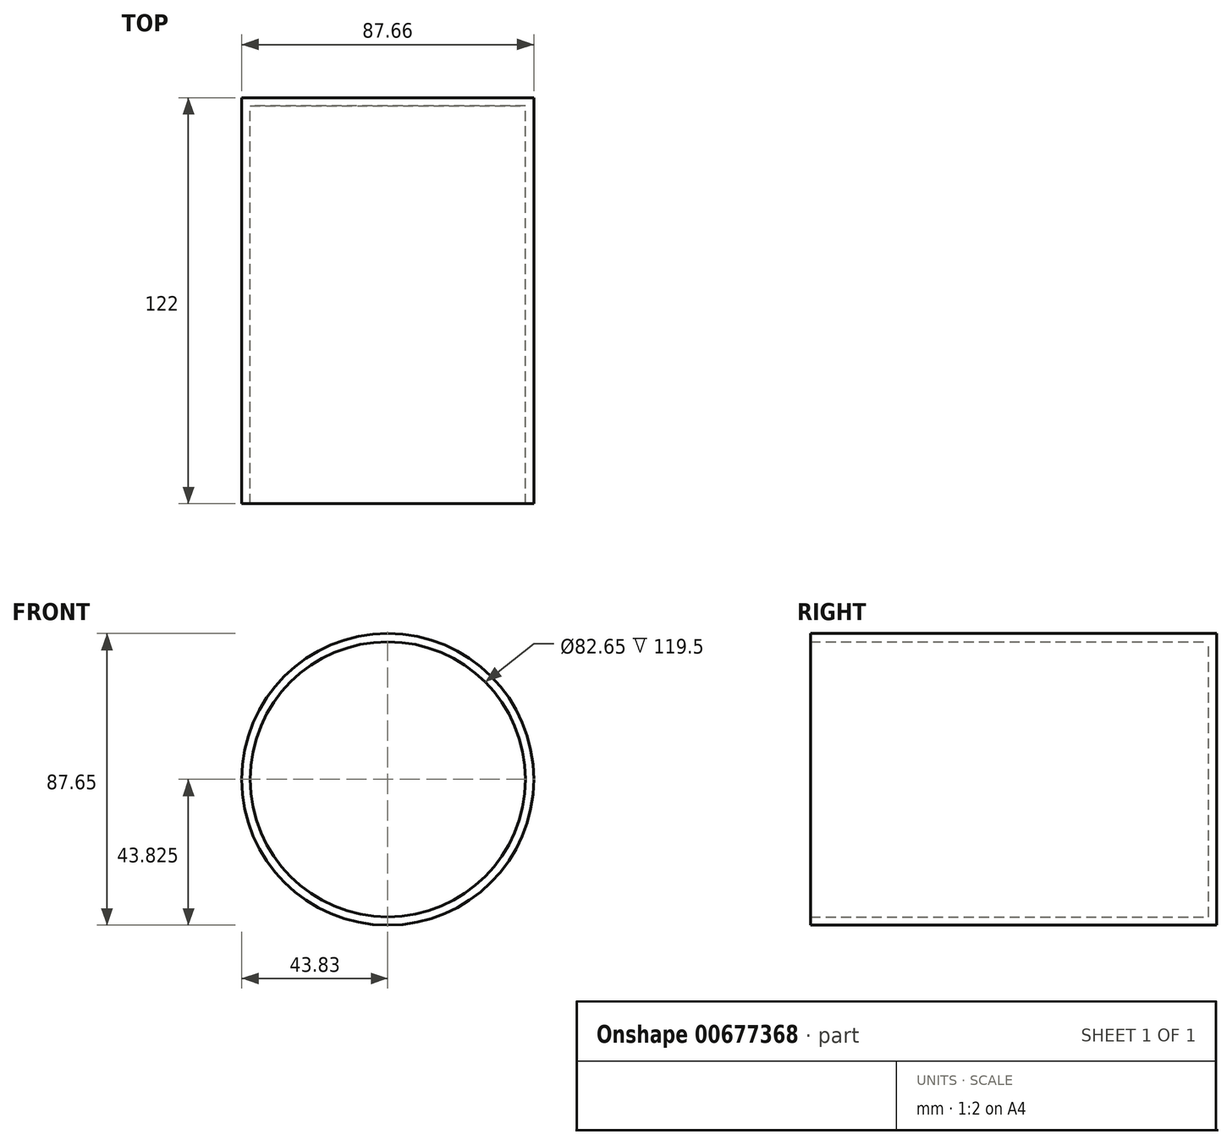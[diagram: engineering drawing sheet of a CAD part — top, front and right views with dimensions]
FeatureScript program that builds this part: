
annotation { "Feature Type Name" : "Feature", "Feature Type Description" : "" }
export const myFeature = defineFeature(function(context is Context, id is Id, definition is map)
    precondition{}
    {
        {
            var Q0;
            Q0=qCreatedBy(makeId("Front.planeOp"),FACE);
            var sketch = newSketch(context, id + "F0", { "sketchPlane" : qUnion([Q0])});
            skArc(sketch, "E0", {"start": v(20.21, 43.5) * mm, "mid": v(-20.49, 89.62) * mm, "end": v(-55.74, 39.2) * mm});
            skLineSegment(sketch, "E1", {"start": v(57.99, 97.4) * mm, "end": v(106.8, 16.13) * mm});
            skFitSpline(sketch, "E2", {"points": [v(-71.55, -93.28) * mm, v(-76.06, -16.4) * mm, v(10.86, -17.02) * mm], "startDerivative": vector(-52.45, 197.28) * mm, "endDerivative": vector(214.59, -42.33) * mm});
            skFitSpline(sketch, "E3.MirrorCS", {"points": [v(-71.55, 93.28) * mm, v(-76.06, 16.4) * mm, v(10.86, 17.02) * mm], "startDerivative": vector(-52.45, -197.28) * mm, "endDerivative": vector(214.59, 42.33) * mm});
            skCircle(sketch, "E4", {"center": v(0, -79.5) * mm, "radius": 43.83 * mm});
            skSolve(sketch);
        }
        {
            var Q0;
            Q0=makeQuery(id+"F0.imprint","IMPRINT",FACE,{"disambiguationData":[TD([[makeQuery(id+"F0.imprint","IMPRINT",EDGE,{"derivedFrom":sQuery(id+"F0.wireOp",EDGE,"E4")}),1.0]])]});
            extrude(context, id + "F1", {"entities" : qUnion([Q0]), "depth" : 122 * mm, "offsetDistance" : 25 * mm});
        }
        {
            var Q0;
            Q0=makeQuery(id+"F1.opExtrude","CAP_FACE",FACE,{"disambiguationData":[OSD([sQuery(id+"F0.wireOp",EDGE,"E4")])],"isStart":false});
            shell(context, id + "F2", {"entities" : qUnion([Q0]), "thickness" : 2.5 * mm});
        }
    });
